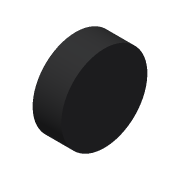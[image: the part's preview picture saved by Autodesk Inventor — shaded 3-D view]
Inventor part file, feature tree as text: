
AUTODESK INVENTOR PART (.ipt)
format: ipt  version: 2019 (Build 230136000, 136)  size: 74,752 bytes
history: native  units: mm
features: other x1, extrude x1, sketch x1
ambient origin geometry x8: Origin, YZ Plane, XZ Plane, XY Plane, X Axis, Y Axis, Z Axis, Center Point
bodies: Body1 (feature_tree)
feature tree (3):
  other  "솔리드1"
  extrude  "돌출1"  Depth=165.0mm
  sketch  "스케치2"
